# Revit family: 14-AS-seddy
name_source: partatom
category: Mechanical Equipment
revit_build: Autodesk Revit 2014 (Build: 20130308_1515(x64)
units: mm (PartAtom-declared; Revit-internal decimal feet)

## types (2) — shared parameters
ASME = Yes
Bottom Connection Diameter = 0.75 "
Bottom Connection Radius = 0.375 "
Flange to Flange Height = 52 "
Flow (GPM) = 2600
Inlet CL to Outlet CL = 30 "
Inlet Pipe Flange Conn = 14 "
Inlet Pipe Flange Conn. Radius = 7 "
Manufacturer = Amtrol
Max Operating Temp = 350 DEG F
Model = 14"-AS
Outlet Pipe Flange Conn = 14 "
Outlet Pipe Flange Conn. Radius = 7 "
Pipe Location off CL = 13 "
Pressure Drop = .6
Tangential = Yes
Tank Diameter = 42 "
Tank Height = 85.125 "
Top Connection Diameter = 0.75 "
Top Connection Radius = 0.375 "
Weight = 2200 lbs

## per-type parameters (varying)
| type | CL to Outlet Flange | Max Operating Pressure | Tank Height Less Stand | Top to Inlet |
| 14-AS 125# W.P. | 26 " | 125 PSI | 71.75 " | 20.875 " |
| 14-AS 150# W.P. 10 BAR | 29 " | 150 PSI | 87 " | 28.5 " |

## geometry (parser evidence)
native form markers: Sweep x1
no freeform markers — native parametric forms only
